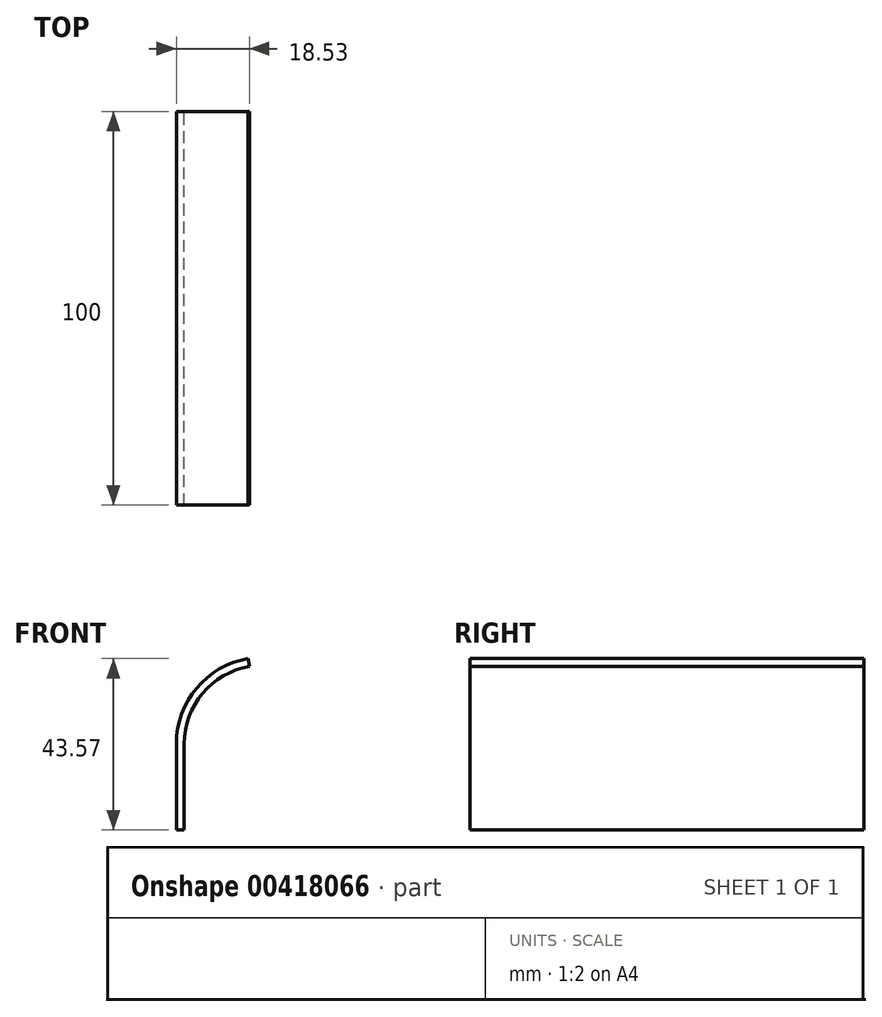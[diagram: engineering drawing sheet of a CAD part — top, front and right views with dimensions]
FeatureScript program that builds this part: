
annotation { "Feature Type Name" : "Feature", "Feature Type Description" : "" }
export const myFeature = defineFeature(function(context is Context, id is Id, definition is map)
    precondition{}
    {
        {
            var Q0;
            Q0=qCreatedBy(makeId("Front.planeOp"),FACE);
            var sketch = newSketch(context, id + "F0", { "sketchPlane" : qUnion([Q0])});
            skArc(sketch, "E0", {"start": v(-3.47, 19.7) * mm, "mid": v(-15.32, 12.86) * mm, "end": v(-20, 0) * mm});
            skArc(sketch, "E1", {"start": v(-3.82, 21.67) * mm, "mid": v(-16.85, 14.14) * mm, "end": v(-22, 0) * mm});
            skLineSegment(sketch, "E2", {"start": v(-20, 0) * mm, "end": v(-20, -21.9) * mm});
            skLineSegment(sketch, "E3", {"start": v(-20, -21.9) * mm, "end": v(-22, -21.9) * mm});
            skLineSegment(sketch, "E4", {"start": v(-22, -21.9) * mm, "end": v(-22, 0) * mm});
            skLineSegment(sketch, "E5", {"start": v(-3.47, 19.7) * mm, "end": v(-3.82, 21.67) * mm});
            skSolve(sketch);
        }
        {
            var Q0;
            Q0 = qSketchRegion(id + "F0", true);
            extrude(context, id + "F1", {"entities" : qUnion([Q0]), "depth" : 100 * mm, "offsetDistance" : 25 * mm});
        }
    });
